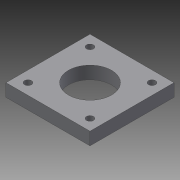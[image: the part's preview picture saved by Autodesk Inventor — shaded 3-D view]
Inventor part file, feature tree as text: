
AUTODESK INVENTOR PART (.ipt)
format: ipt  version: 2015 (Build 190159000, 159)  size: 89,088 bytes
history: native  units: in
note: dims shown in document units (in); Inventor stores cm internally (conversion verified against a paired STEP export)
features: extrude x1, sketch x1
ambient origin geometry x8: Origin, YZ Plane, XZ Plane, XY Plane, X Axis, Y Axis, Z Axis, Center Point
bodies: Body1 (feature_tree)
feature tree (2):
  extrude  "Extrusion4"  Depth=1.6535in
  sketch  "Sketch1"  dims[d0=1.6535in d1=1.6535in d4=0.1378in d8=0.8465in d11=0.25in d12=0.0in d13=1.2205in]
